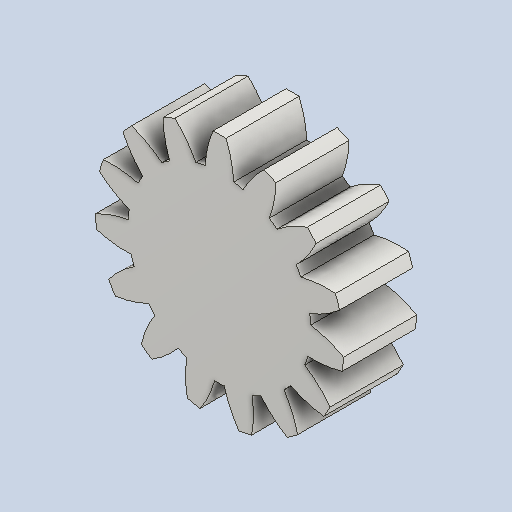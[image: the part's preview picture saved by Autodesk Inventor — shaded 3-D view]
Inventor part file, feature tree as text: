
AUTODESK INVENTOR PART (.ipt)
format: ipt  version: 2024 (Build 280153000, 153)  size: 223,232 bytes
history: native  units: mm (DEFAULTED — no unit token found)
features: plane x3, other x3, extrude x1, sketch x1
ambient origin geometry x8: Origin, YZ Plane, XZ Plane, XY Plane, X Axis, Y Axis, Z Axis, Center Point
bodies: Solid1 (feature_tree)
feature tree (8):
  extrude  "Extrusion1"  Depth=10.0mm TaperAngle=0.0deg
  plane  "Work Plane2"
  plane  "Work Plane8"
  plane  "Work Plane9"
  other  "Spur Gear"
  sketch  "Sketch1"  dims[d0=34.0mm d1=10.0mm d2=0.0mm d3=30.0mm d4=10.0mm d5=0.0mm d16=25.0mm d17=0.0mm d34=2.094395mm d39=0.0mm d41=0.0mm d43=25.0mm d46=25.0mm d47=0.0mm d48=0.0mm]
  other  "Srf1"
  other  "Pitch Diameter"
